# Revit family: NBS_WallgateLtd_ShwrMxrs_PBA050-51-SHWR
name_source: partatom
category: Plumbing Fixtures
revit_build: Autodesk Revit 2014 (Build: 20130709_2115(x64)
units: mm (PartAtom-declared; Revit-internal decimal feet)

## types (2) — shared parameters
AssetType = Fixed
BodyMaterial = Stainless steel
CableLength = 4000 mm
Description = Electronic activation single flush WC piezo touch button
DurationUnit = year
Features = Anti-ligature design, highly vandal-resistant
Finish = Stainless steel
HasIntegralShutOffDevice = No
IfcExportAs = IfcValveType
IfcExportType = FLUSHING
IntegralAccessoryOptions = CISTFV Electronic cisterns, FVA Non-Potable Direct Flush Valves, DFKIT Potable Direct Flush Valves, WVC Flush Valve Cables, WDC Electronic Controllers, WVPS Shower Water Valve Pack, MV0001 Thermostatic Mixer Valve
IsHighPressure = No
ManufacturerName = Wallgate Ltd
ManufacturerURL = www.wallgate.com
NBSCertification = www.nationalbimlibrary.com/cert/2uvif5zq
NBSDescription = WC flushing valves
NBSReference = 45-35-70/389
NominalHeight = 38 mm
NominalWidth = 38 mm
Operation = Piezo push button
ProductInformation = www.wallgate.com/document-centre/docmenu-washroom-controls/docmenu-controls-piezo-activation/doccat-piezo-activation-buttons
Size = 21.0
TestPressure = 0.0
ThirdPartyCertification = Ministry of Justice Safer Cell Approval
Uniclass2 = 45-31-93/491
ValveMechanism = Unset
ValveOperation = Other
Version = 3
WarrantyDurationParts = 1
WarrantyDurationUnit = year
Weight = 0.25 kg
zero-valued in all types: CloseOffRating, FlowCoefficient, FlushingRate

## per-type parameters (varying)
| type | BIMObjectName | Name | NominalLength | WallThicknessOptions | WaterSupplyFittingMaterial |
| PBA050-CWC | NBS_WallgateLtd_WCFlushingValves_PBA050-CWC | WCFlushingValves_PBA050-CWC_WallgateLtd | 98 mm  [stored 0.321522 ft] | 10-85 mm | NBS_Concept |
| PBA051-CWC | NBS_WallgateLtd_WCFlushingValves_PBA051-CWC | WCFlushingValves_PBA051-CWC_Wallgate | 203 mm | 85-190 mm | <By Category> |

note: column(s) folded — value = type name in every type: ModelNumber

note: [stored X ft] marks values corroborated as IEEE doubles in the binary element streams (Revit-internal decimal feet)

## geometry (parser evidence)
native form markers: Sweep x5
no freeform markers — native parametric forms only
